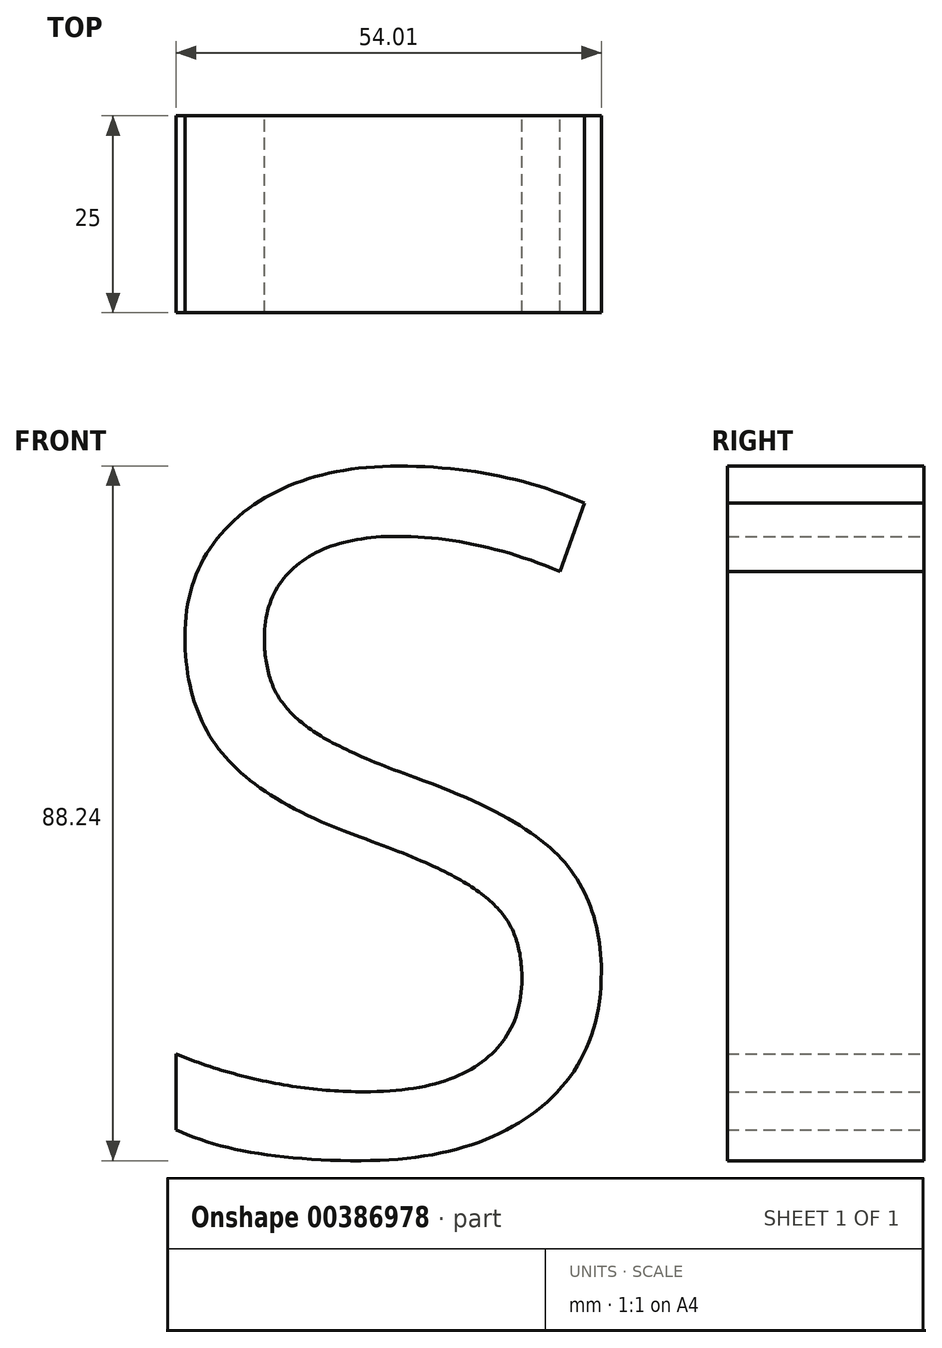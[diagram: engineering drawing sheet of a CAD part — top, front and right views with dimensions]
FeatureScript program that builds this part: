
annotation { "Feature Type Name" : "Feature", "Feature Type Description" : "" }
export const myFeature = defineFeature(function(context is Context, id is Id, definition is map)
    precondition{}
    {
        {
            var Q0;
            Q0=qCreatedBy(makeId("Front.planeOp"),FACE);
            var sketch = newSketch(context, id + "F0", { "sketchPlane" : qUnion([Q0])});
            skText(sketch, "E0", { "text": "S", "fontName": "OpenSans-Regular.ttf"});
            const initialGuessF0  = {"E0": [-0.03587, -0.04844, 1, 0, 0.08657]};
            skSetInitialGuess(sketch, initialGuessF0);
            skSolve(sketch);
        }
        {
            var Q0;
            Q0 = qSketchRegion(id + "F0", true);
            extrude(context, id + "F1", {"entities" : qUnion([Q0]), "depth" : 25 * mm});
        }
    });
